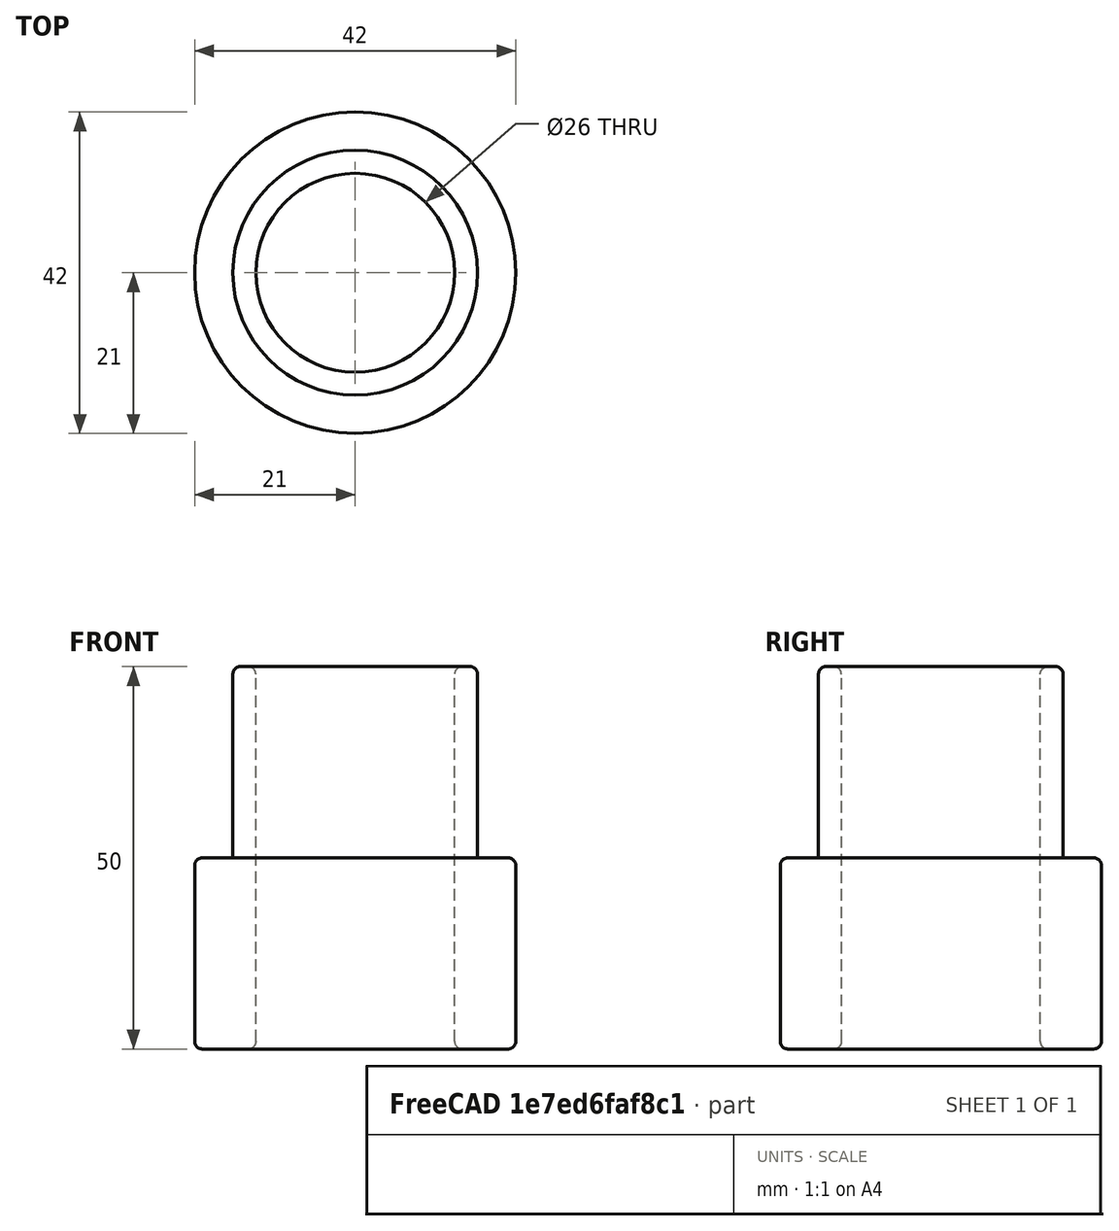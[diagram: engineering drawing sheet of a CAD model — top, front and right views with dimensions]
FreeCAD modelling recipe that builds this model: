
FCSTD DOCUMENT  (FreeCAD 0.14R2935 (Git))
Label: pool-connector-32-42
License: CC-BY 3.0
LicenseURL: http://creativecommons.org/licenses/by/3.0/
objects: Part::Cylinder×4, Part::Cut×2, Part::Fillet×2, Part::MultiFuse×1
note: 9 computed .brp shape members not serialized (recipe doc carries the construction recipe); baked Part::Feature solids carry a one-line shape summary decoded from their .brp

FEATURE [Part::Cylinder] Cylinder  label="Outer 42 mm"
  Angle = 360
  Height = 25
  Radius = 21
FEATURE [Part::Cylinder] Cylinder001  label="Ydre 32"
  Angle = 360
  Height = 50
  Radius = 16
FEATURE [Part::Cylinder] Cylinder002  label="Indre hul"
  Angle = 360
  Height = 120
  Placement = pos=(0,0,-60) rot=(0,0,1;0rad)
  Radius = 13
FEATURE [Part::Cut] Cut
  Base = -> Cylinder001
  Tool = -> Cylinder002
FEATURE [Part::Cylinder] Cylinder003  label="Indre hul001"
  Angle = 360
  Height = 120
  Placement = pos=(0,0,-60) rot=(0,0,1;0rad)
  Radius = 16
FEATURE [Part::Cut] Cut001
  Base = -> Cylinder
  Tool = -> Cylinder003
FEATURE [Part::Fillet] Fillet
  Base = -> Cut001
  Edges = 2 edges r=1: [Edge1,Edge3]
FEATURE [Part::Fillet] Fillet001
  Base = -> Cut
  Edges = 3 edges r=1: [Edge1,Edge4,Edge5]
FEATURE [Part::MultiFuse] Fusion
  Shapes = -> [Fillet,Fillet001]
